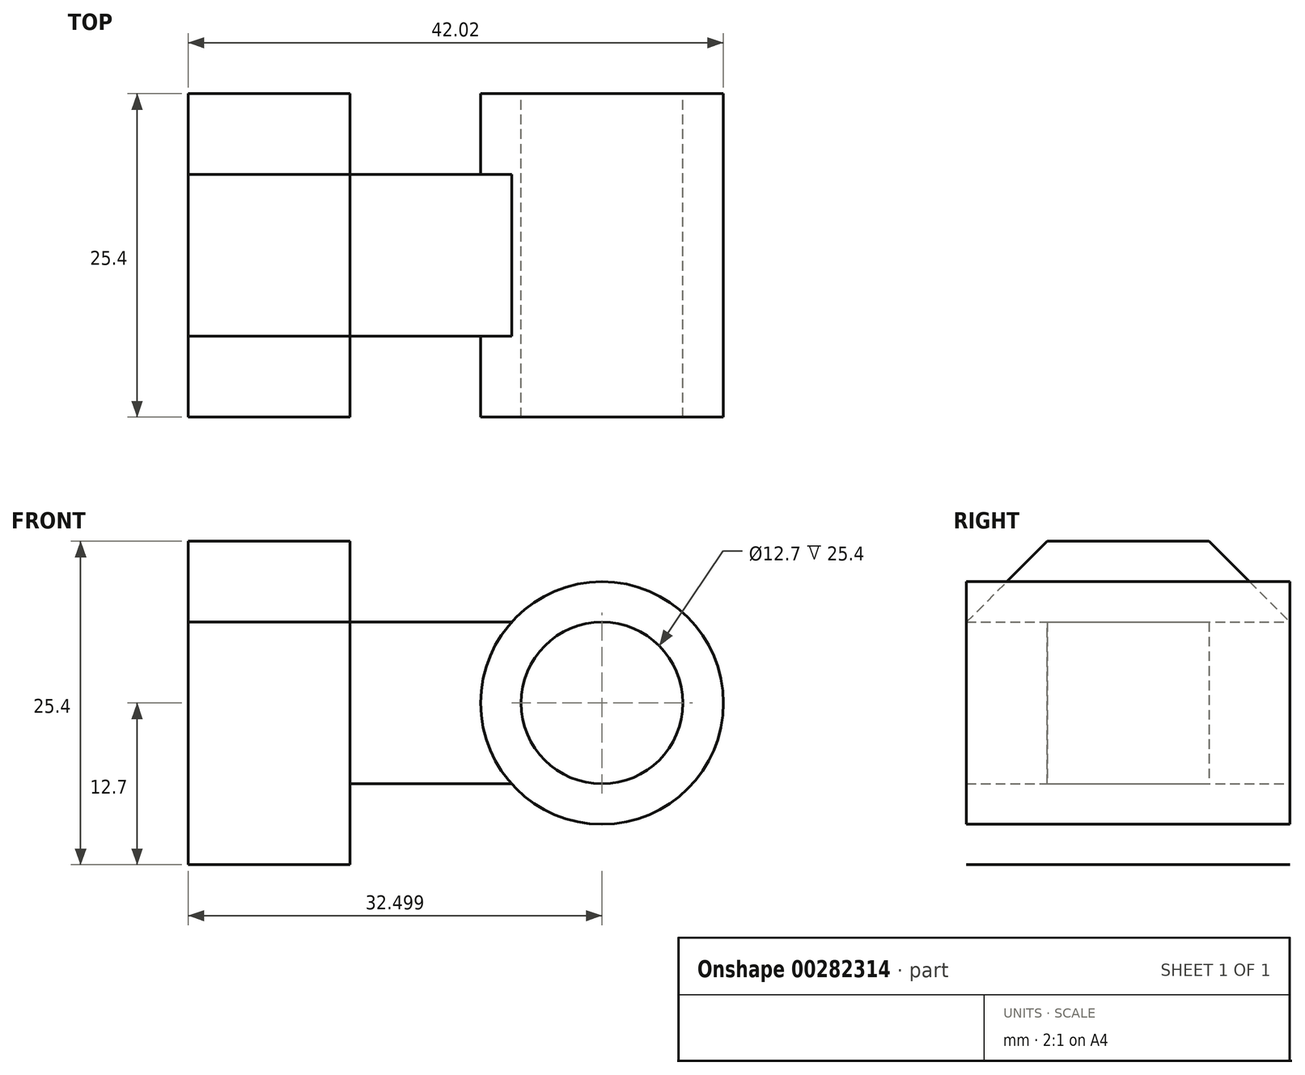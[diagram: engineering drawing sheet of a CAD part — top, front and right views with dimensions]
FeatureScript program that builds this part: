
annotation { "Feature Type Name" : "Feature", "Feature Type Description" : "" }
export const myFeature = defineFeature(function(context is Context, id is Id, definition is map)
    precondition{}
    {
        {
            var Q0;
            Q0=qCreatedBy(makeId("Right.planeOp"),FACE);
            var sketch = newSketch(context, id + "F0", { "sketchPlane" : qUnion([Q0])});
            skLineSegment(sketch, "E0", {"start": v(0, 0) * mm, "end": v(25.4, 0) * mm});
            skLineSegment(sketch, "E1", {"start": v(25.4, 0) * mm, "end": v(25.4, 19.05) * mm});
            skLineSegment(sketch, "E2", {"start": v(0, 19.05) * mm, "end": v(0, 0) * mm});
            skLineSegment(sketch, "E3", {"start": v(0, 19.05) * mm, "end": v(6.35, 25.4) * mm});
            skLineSegment(sketch, "E4", {"start": v(19.05, 25.4) * mm, "end": v(25.4, 19.05) * mm});
            skLineSegment(sketch, "E5", {"start": v(6.35, 25.4) * mm, "end": v(19.05, 25.4) * mm});
            skSolve(sketch);
        }
        {
            var Q0;
            Q0 = qSketchRegion(id + "F0", true);
            extrude(context, id + "F1", {"entities" : qUnion([Q0]), "depth" : 12.7 * mm});
        }
        {
            var Q0;
            Q0=makeQuery(id+"F1.opExtrude","CAP_FACE",FACE,{"disambiguationData":[OSD([sQuery(id+"F0.wireOp",EDGE,"E0"),sQuery(id+"F0.wireOp",EDGE,"E1"),sQuery(id+"F0.wireOp",EDGE,"E2"),sQuery(id+"F0.wireOp",EDGE,"E3"),sQuery(id+"F0.wireOp",EDGE,"E4"),sQuery(id+"F0.wireOp",EDGE,"E5")])],"isStart":false});
            var sketch = newSketch(context, id + "F2", { "sketchPlane" : qUnion([Q0])});
            skLineSegment(sketch, "E6", {"start": v(6.35, 6.35) * mm, "end": v(6.35, 19.05) * mm});
            skLineSegment(sketch, "E7", {"start": v(6.35, 19.05) * mm, "end": v(19.05, 19.05) * mm});
            skLineSegment(sketch, "E8", {"start": v(19.05, 19.05) * mm, "end": v(19.05, 6.35) * mm});
            skLineSegment(sketch, "E9", {"start": v(6.35, 6.35) * mm, "end": v(19.05, 6.35) * mm});
            skSolve(sketch);
        }
        {
            var Q0;
            Q0=makeQuery(id+"F2.imprint","IMPRINT",FACE,{"disambiguationData":[TD([[makeQuery(id+"F2.imprint","IMPRINT",EDGE,{"derivedFrom":sQuery(id+"F2.wireOp",EDGE,"E6")}),-1.0]])]});
            extrude(context, id + "F3", {"entities" : qUnion([Q0]), "operationType" : NewBodyOperationType.ADD, "depth" : 25.4 * mm});
        }
        {
            var Q0;
            Q0=makeQuery(id+"F3.opExtrude","SWEPT_FACE",FACE,{"disambiguationData":[OSD([sQuery(id+"F2.wireOp",EDGE,"E6")])]});
            var sketch = newSketch(context, id + "F4", { "sketchPlane" : qUnion([Q0])});
            skLineSegment(sketch, "E10", {"start": v(38.1, 19.05) * mm, "end": v(25.4, 19.05) * mm});
            skLineSegment(sketch, "E11", {"start": v(38.1, 19.05) * mm, "end": v(38.1, 6.35) * mm});
            skLineSegment(sketch, "E12", {"start": v(38.1, 6.35) * mm, "end": v(25.4, 6.35) * mm});
            skArc(sketch, "E13", {"start": v(25.4, 19.05) * mm, "mid": v(22.97, 12.7) * mm, "end": v(25.4, 6.35) * mm});
            skSolve(sketch);
        }
        {
            var Q0;
            Q0 = qSketchRegion(id + "F4", true);
            extrude(context, id + "F5", {"entities" : qUnion([Q0]), "operationType" : NewBodyOperationType.REMOVE, "oppositeDirection" : true, "depth" : 12.7 * mm});
        }
        {
            var Q0;
            Q0=makeQuery(id+"F3.opExtrude","SWEPT_FACE",FACE,{"disambiguationData":[OSD([sQuery(id+"F2.wireOp",EDGE,"E6")])]});
            var sketch = newSketch(context, id + "F6", { "sketchPlane" : qUnion([Q0])});
            skCircle(sketch, "E14", {"center": v(32.5, 12.7) * mm, "radius": 9.53 * mm});
            skSolve(sketch);
        }
        {
            var Q0;
            Q0 = qSketchRegion(id + "F6", true);
            extrude(context, id + "F7", {"entities" : qUnion([Q0]), "depth" : 6.35 * mm});
        }
        {
            var Q0;
            Q0=makeQuery(id+"F7.opExtrude","CAP_FACE",FACE,{"disambiguationData":[OSD([sQuery(id+"F6.wireOp",EDGE,"E14")])],"isStart":true});
            extrude(context, id + "F8", {"entities" : qUnion([Q0]), "operationType" : NewBodyOperationType.ADD, "depth" : 19.05 * mm});
        }
        {
            var Q0;
            Q0=makeQuery(id+"F8.opExtrude","CAP_FACE",FACE,{"disambiguationData":[OSD([sQuery(id+"F6.wireOp",EDGE,"E14")])],"isStart":false});
            var sketch = newSketch(context, id + "F9", { "sketchPlane" : qUnion([Q0])});
            skCircle(sketch, "E15", {"center": v(-32.5, 12.7) * mm, "radius": 6.35 * mm});
            skSolve(sketch);
        }
        {
            var Q0;
            Q0 = qSketchRegion(id + "F9", true);
            extrude(context, id + "F10", {"entities" : qUnion([Q0]), "operationType" : NewBodyOperationType.REMOVE, "oppositeDirection" : true, "depth" : 25.4 * mm});
        }
    });
